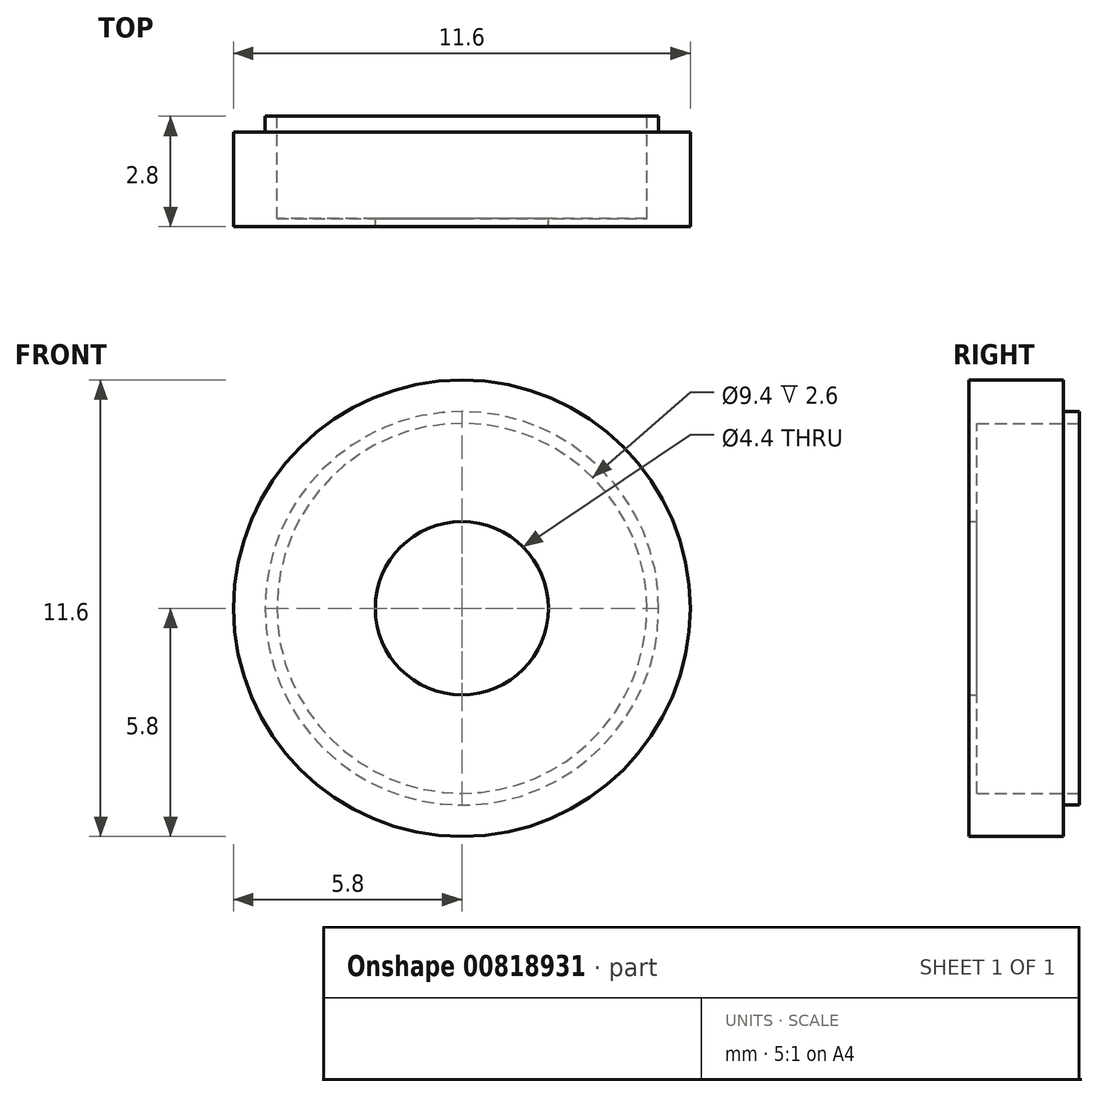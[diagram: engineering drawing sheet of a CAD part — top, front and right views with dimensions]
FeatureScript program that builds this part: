
annotation { "Feature Type Name" : "Feature", "Feature Type Description" : "" }
export const myFeature = defineFeature(function(context is Context, id is Id, definition is map)
    precondition{}
    {
        {
            var Q0;
            Q0=qCreatedBy(makeId("Front.planeOp"),FACE);
            var sketch = newSketch(context, id + "F0", { "sketchPlane" : qUnion([Q0])});
            skCircle(sketch, "E0", {"center": v(0, 0) * mm, "radius": 5.8 * mm});
            skSolve(sketch);
        }
        {
            var Q0;
            Q0=makeQuery(id+"F0.imprint","IMPRINT",FACE,{"disambiguationData":[TD([[makeQuery(id+"F0.imprint","IMPRINT",EDGE,{"derivedFrom":sQuery(id+"F0.wireOp",EDGE,"E0")}),1.0]])]});
            var Q1;
            Q1=qSketchRegion(id+"F2",true);
            extrude(context, id + "F1", {"entities" : qUnion([Q0, Q1]), "depth" : 1.8 * mm, "offsetDistance" : 25 * mm});
        }
        {
            var Q0;
            Q0=makeQuery(id+"F1.opExtrude","CAP_FACE",FACE,{"disambiguationData":[OSD([sQuery(id+"F0.wireOp",EDGE,"E0")])],"isStart":false});
            var sketch = newSketch(context, id + "F2", { "sketchPlane" : qUnion([Q0])});
            skCircle(sketch, "E1", {"center": v(0, 0) * mm, "radius": 5.8 * mm});
            skCircle(sketch, "E2", {"center": v(0, 0) * mm, "radius": 4.7 * mm});
            skSolve(sketch);
        }
        {
            var Q0;
            Q0=makeQuery(id+"F2.imprint","IMPRINT",FACE,{"disambiguationData":[TD([[makeQuery(id+"F2.imprint","IMPRINT",EDGE,{"derivedFrom":sQuery(id+"F2.wireOp",EDGE,"E1")}),1.0]])]});
            extrude(context, id + "F3", {"entities" : qUnion([Q0]), "operationType" : NewBodyOperationType.ADD, "depth" : 0.4 * mm, "offsetDistance" : 25 * mm});
        }
        {
            var Q0;
            Q0=makeQuery(id+"F1.opExtrude","CAP_FACE",FACE,{"disambiguationData":[OSD([sQuery(id+"F0.wireOp",EDGE,"E0")])],"isStart":false});
            var sketch = newSketch(context, id + "F4", { "sketchPlane" : qUnion([Q0])});
            skCircle(sketch, "E3", {"center": v(0, 0) * mm, "radius": 4.7 * mm});
            skSolve(sketch);
        }
        {
            var Q0;
            Q0=makeQuery(id+"F4.imprint","IMPRINT",FACE,{"disambiguationData":[TD([[makeQuery(id+"F4.imprint","IMPRINT",EDGE,{"derivedFrom":sQuery(id+"F4.wireOp",EDGE,"E3")}),1.0]])]});
            extrude(context, id + "F5", {"entities" : qUnion([Q0]), "operationType" : NewBodyOperationType.REMOVE, "oppositeDirection" : true, "depth" : 1.8 * mm, "offsetDistance" : 25 * mm});
        }
        {
            var Q0;
            Q0=makeQuery(id+"F3.opExtrude","CAP_FACE",FACE,{"disambiguationData":[OSD([sQuery(id+"F2.wireOp",EDGE,"E1"),sQuery(id+"F2.wireOp",EDGE,"E2")])],"isStart":false});
            var sketch = newSketch(context, id + "F6", { "sketchPlane" : qUnion([Q0])});
            skCircle(sketch, "E4", {"center": v(0, 0) * mm, "radius": 5.8 * mm});
            skCircle(sketch, "E5", {"center": v(0, 0) * mm, "radius": 2.2 * mm});
            skSolve(sketch);
        }
        {
            var Q0;
            Q0=makeQuery(id+"F6.imprint","IMPRINT",FACE,{"disambiguationData":[TD([[makeQuery(id+"F6.imprint","IMPRINT",EDGE,{"derivedFrom":sQuery(id+"F6.wireOp",EDGE,"E4")}),1.0]])]});
            var Q1;
            Q1=makeQuery(id+"F6.imprint","IMPRINT",FACE,{"disambiguationData":[TD([[makeQuery(id+"F6.imprint","IMPRINT",EDGE,{"derivedFrom":sQuery(id+"F6.wireOp",EDGE,"E5")}),-1.0]])]});
            extrude(context, id + "F7", {"entities" : qUnion([Q0, Q1]), "operationType" : NewBodyOperationType.ADD, "depth" : 0.2 * mm, "offsetDistance" : 25 * mm});
        }
        {
            var Q0;
            Q0=makeQuery(id+"F1.opExtrude","CAP_FACE",FACE,{"disambiguationData":[OSD([sQuery(id+"F0.wireOp",EDGE,"E0")])],"isStart":true});
            var sketch = newSketch(context, id + "F8", { "sketchPlane" : qUnion([Q0])});
            skCircle(sketch, "E6", {"center": v(0, 0) * mm, "radius": 5 * mm});
            skSolve(sketch);
        }
        {
            var Q0;
            Q0=makeQuery(id+"F8.imprint","IMPRINT",FACE,{"disambiguationData":[TD([[makeQuery(id+"F8.imprint","IMPRINT",EDGE,{"derivedFrom":sQuery(id+"F8.wireOp",EDGE,"E6")}),1.0]])]});
            extrude(context, id + "F9", {"entities" : qUnion([Q0]), "operationType" : NewBodyOperationType.ADD, "depth" : 0.4 * mm, "offsetDistance" : 25 * mm});
        }
    });
